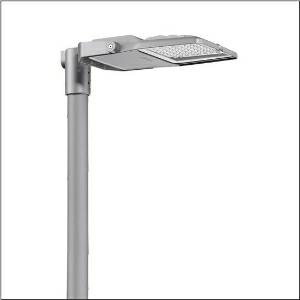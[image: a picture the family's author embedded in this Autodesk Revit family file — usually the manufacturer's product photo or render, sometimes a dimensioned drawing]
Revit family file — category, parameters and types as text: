
# Revit family: floodlight_fl_21_iq_mini___pl64_5xa7772c2e3a_d31a
name_source: partatom
category: Lighting Fixtures
units: mm (PartAtom-declared; Revit-internal decimal feet)

## family parameters
Cut with Voids When Loaded = No
Host = Face
Light Source = No
Part Type = Normal
Room Calculation Point = No
Round Connector Dimension = Use Diameter
Shared = No

## types (1)
- --- (1 x LED, 11790 lm, 87.2 W, 3000K)
    Apparent Load = 87 VA
    CIE Flux Codes = 28 80 98 100 100
    Color Rendering = 70
    Color Temperature = 3000K
    Default Elevation = 1800 mm
    Description = Floodlight FL 21 iQ mini, floodlight, primary light control with lens, of PMMA, primary optical cover: protective disc, of toughened safety glass, transparent, light distribution: PL64, light emission: direct distribution, installation type: surface-mounted, LED, High Power LED, rated luminous flux: 11.790lm, luminous efficacy: 135lm/W, light colour: 730, colour temperature: 3000K, control gear: iQ Street-Remote/DALI, control: Street-Remote, Auto-Match, Temp-Guard, Night-Set, Smart-Wire, optimised constant luminous flux control (CLO 2.0), Light-Fading, Lumen-Switch, with terminal, 6-pole, mains connection: 220..240V, AC, 50/60Hz, start of lifetime: 87W, end of service life: 92W, reduction: 40W, luminaire housing, of diecast aluminium, powder-coated, Siteco® metallic grey (DB 702S), corrosivity category C5 mid according to DIN EN ISO 12944, suitable for swimming pools, chlorine-resistant, sealing non-destructively replaceable, please order mast flange separately, mast bracket, of steel, galvanised, powder-coated, protection rating (complete): IP66, insulation class (complete): insulation class II (safety insulation), certification: CE, ENEC, VDE, protection symbol: D, impact resistance: IK08, permissible operating ambient temperature: -40..+40°C, permissible operating ambient temperature for outdoor applications: -40..+50°C, standard: DIN EN 12944, LABS conformity tested according to VDMA 24364:2018-05, packaging unit: 1 piece

Light Distribution: PL64
    Height = 70 mm
    Lamp = 1 x LED
    Lamp Light Flux = 11790 lm
    Lamp Power = 87.2 W
    Lamp count = 1
    Length = 485 mm
    Luminous efficacy = 135 lm/W
    Manufacturer = Siteco
    ModVariant = No
    Model = 5XA7772C2E3A
    Number of Poles = 1
    OnlyDefault = Yes
    Power Factor = 1
    Product Name = Floodlight FL 21 iQ mini | PL64
    Product group = floodlight | pylon annexe
    ProductGroupID = 6201
    Protection Class = Protection class II
    Protection Degree = IP 66
    RLX_Detail_Level = 1
    RLX_Emergency_Light_Flux = 0 lm
    RLX_Emergency_Type = 0
    RLX_Emergency_Type_DB = No
    RlxData = <blob elided: 101277 chars, md5=7d35b0f8>
    Socket = socket
    Standby Power = 0 W
    System Light Flux = 11790 lm
    System Power = 87 W
    Type Comments = factory setting: luminous flux: 100 % | dim-lin: 254 | 456 mA
    Type Image = l_1007125.jpg
    URL = http://relux.com
    VarID = @adj_187827
    Voltage = 0 V
    Weight = 0.00 kg
    Width = 337 mm

## geometry (parser evidence)
native form markers: Blend x4, Sweep x11
no freeform markers — native parametric forms only
